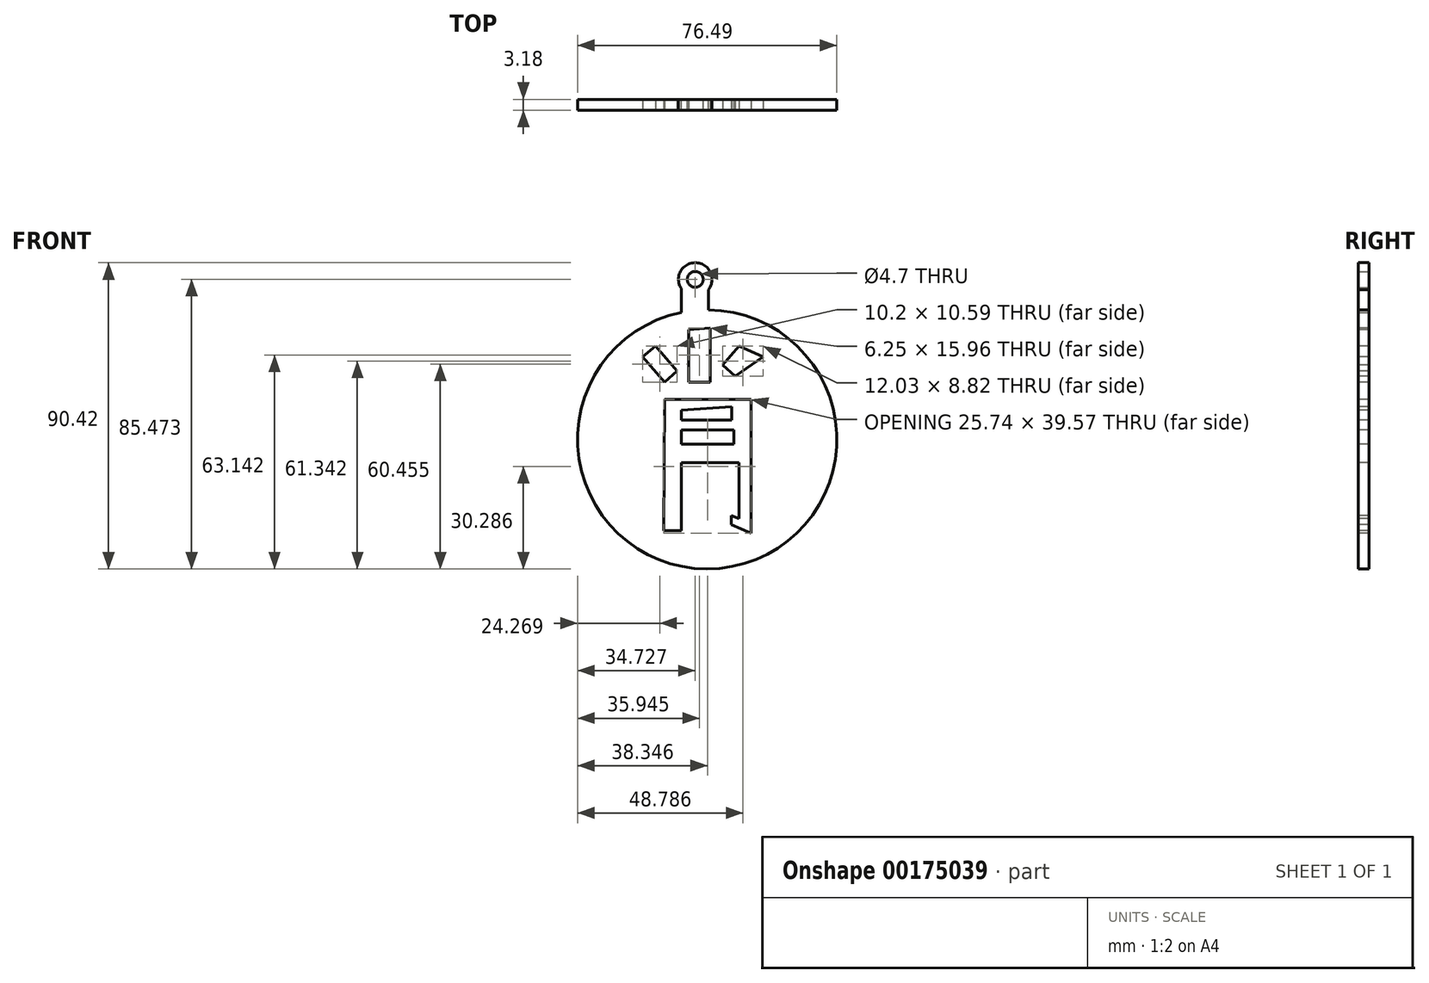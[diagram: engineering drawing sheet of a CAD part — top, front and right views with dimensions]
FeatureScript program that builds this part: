
annotation { "Feature Type Name" : "Feature", "Feature Type Description" : "" }
export const myFeature = defineFeature(function(context is Context, id is Id, definition is map)
    precondition{}
    {
        {
            var Q0;
            Q0=qCreatedBy(makeId("Front.planeOp"),FACE);
            var sketch = newSketch(context, id + "F0", { "sketchPlane" : qUnion([Q0])});
            skCircle(sketch, "E0", {"center": v(39.43, 36.64) * mm, "radius": 38.25 * mm});
            skLineSegment(sketch, "E1", {"start": v(31.77, 74.12) * mm, "end": v(31.77, 81.17) * mm});
            skLineSegment(sketch, "E2", {"start": v(39.78, 74.89) * mm, "end": v(39.78, 80.8) * mm});
            skCircle(sketch, "E3", {"center": v(35.9, 83.87) * mm, "radius": 4.94 * mm});
            skCircle(sketch, "E4", {"center": v(35.9, 83.87) * mm, "radius": 2.35 * mm});
            skSolve(sketch);
        }
        {
            var Q0;
            Q0 = qSketchRegion(id + "F0", true);
            extrude(context, id + "F1", {"entities" : qUnion([Q0]), "depth" : 3.17 * mm});
        }
        {
            var Q0;
            Q0=makeQuery(id+"F1.opExtrude","CAP_FACE",FACE,{"disambiguationData":[OSD([sQuery(id+"F0.wireOp",EDGE,"E0"),sQuery(id+"F0.wireOp",EDGE,"E1"),sQuery(id+"F0.wireOp",EDGE,"E2"),sQuery(id+"F0.wireOp",EDGE,"E3"),sQuery(id+"F0.wireOp",EDGE,"E4")])],"isStart":false});
            var sketch = newSketch(context, id + "F2", { "sketchPlane" : qUnion([Q0])});
            skLineSegment(sketch, "E5", {"start": v(20.35, 60.96) * mm, "end": v(26.83, 53.56) * mm});
            skLineSegment(sketch, "E6", {"start": v(26.83, 53.56) * mm, "end": v(30.55, 56.81) * mm});
            skLineSegment(sketch, "E7", {"start": v(30.55, 56.81) * mm, "end": v(24.13, 64.15) * mm});
            skLineSegment(sketch, "E8", {"start": v(24.13, 64.15) * mm, "end": v(20.35, 60.96) * mm});
            skLineSegment(sketch, "E9", {"start": v(34, 69.06) * mm, "end": v(34, 53.56) * mm});
            skLineSegment(sketch, "E10", {"start": v(34, 53.56) * mm, "end": v(40.25, 53.56) * mm});
            skLineSegment(sketch, "E11", {"start": v(40.25, 53.56) * mm, "end": v(40.25, 69.52) * mm});
            skLineSegment(sketch, "E12", {"start": v(40.25, 69.52) * mm, "end": v(34, 69.06) * mm});
            skLineSegment(sketch, "E13", {"start": v(48.8, 64.15) * mm, "end": v(43.95, 58.65) * mm});
            skLineSegment(sketch, "E14", {"start": v(43.95, 58.65) * mm, "end": v(47.7, 55.33) * mm});
            skLineSegment(sketch, "E15", {"start": v(47.7, 55.33) * mm, "end": v(55.98, 60.96) * mm});
            skLineSegment(sketch, "E16", {"start": v(55.98, 60.96) * mm, "end": v(48.8, 64.15) * mm});
            skLineSegment(sketch, "E17", {"start": v(26.83, 48.47) * mm, "end": v(52.4, 48.47) * mm});
            skPoint(sketch, "E17.endSnap0", {"position": v(52.4, 62.56) * mm});
            skLineSegment(sketch, "E18", {"start": v(52.4, 48.47) * mm, "end": v(52.4, 8.9) * mm});
            skLineSegment(sketch, "E19", {"start": v(52.4, 8.9) * mm, "end": v(46.55, 11.5) * mm});
            skLineSegment(sketch, "E20", {"start": v(46.55, 11.5) * mm, "end": v(46.55, 14.23) * mm});
            skLineSegment(sketch, "E21", {"start": v(46.55, 14.23) * mm, "end": v(48.8, 13.22) * mm});
            skLineSegment(sketch, "E22", {"start": v(48.8, 13.22) * mm, "end": v(48.8, 29.73) * mm});
            skLineSegment(sketch, "E23", {"start": v(48.8, 29.73) * mm, "end": v(31.77, 29.73) * mm});
            skLineSegment(sketch, "E24", {"start": v(31.77, 29.73) * mm, "end": v(31.77, 9.68) * mm});
            skLineSegment(sketch, "E25", {"start": v(31.77, 9.68) * mm, "end": v(26.66, 9.68) * mm});
            skLineSegment(sketch, "E26", {"start": v(26.66, 9.68) * mm, "end": v(26.83, 48.47) * mm});
            skLineSegment(sketch, "E27", {"start": v(31.77, 35.29) * mm, "end": v(47.27, 35.29) * mm});
            skLineSegment(sketch, "E28", {"start": v(47.27, 35.29) * mm, "end": v(47.27, 39.38) * mm});
            skLineSegment(sketch, "E29", {"start": v(47.27, 39.38) * mm, "end": v(31.77, 39.38) * mm});
            skLineSegment(sketch, "E30", {"start": v(31.77, 39.38) * mm, "end": v(31.77, 35.29) * mm});
            skLineSegment(sketch, "E31", {"start": v(31.77, 45.27) * mm, "end": v(31.77, 42.32) * mm});
            skLineSegment(sketch, "E32", {"start": v(31.77, 42.32) * mm, "end": v(46.62, 42.32) * mm});
            skLineSegment(sketch, "E33", {"start": v(46.62, 42.32) * mm, "end": v(46.62, 46.25) * mm});
            skLineSegment(sketch, "E34", {"start": v(46.62, 46.25) * mm, "end": v(31.77, 45.27) * mm});
            skLineSegment(sketch, "E35", {"start": v(36.15, 35.29) * mm, "end": v(34.36, 35.29) * mm});
            skPoint(sketch, "E36.startSnap0", {"position": v(39.52, 39.38) * mm});
            skSolve(sketch);
        }
        {
            var Q0;
            Q0=makeQuery(id+"F2.imprint","IMPRINT",FACE,{"disambiguationData":[TD([[makeQuery(id+"F2.imprint","IMPRINT",EDGE,{"derivedFrom":sQuery(id+"F2.wireOp",EDGE,"E5")}),1.0]])]});
            var Q1;
            Q1=makeQuery(id+"F2.imprint","IMPRINT",FACE,{"disambiguationData":[TD([[makeQuery(id+"F2.imprint","IMPRINT",EDGE,{"derivedFrom":sQuery(id+"F2.wireOp",EDGE,"E9")}),1.0]])]});
            var Q2;
            Q2=makeQuery(id+"F2.imprint","IMPRINT",FACE,{"disambiguationData":[TD([[makeQuery(id+"F2.imprint","IMPRINT",EDGE,{"derivedFrom":sQuery(id+"F2.wireOp",EDGE,"E13")}),1.0]])]});
            var Q3;
            Q3=makeQuery(id+"F2.imprint","IMPRINT",FACE,{"disambiguationData":[TD([[makeQuery(id+"F2.imprint","IMPRINT",EDGE,{"derivedFrom":sQuery(id+"F2.wireOp",EDGE,"E17")}),-1.0]])]});
            var Q4;
            {var subQ0=sQuery(id+"F2.wireOp",EDGE,"aVBbDBSk-wFVR-j3cv-Srhj-Kdv2nJzsByz3");Q4=makeQuery(id+"F2.imprint","IMPRINT",FACE,{"disambiguationData":[TD([[makeQuery(id+"F2.imprint","IMPRINT",EDGE,{"derivedFrom":subQ0}),1.0]])]});}
            var Q5;
            {var subQ0=sQuery(id+"F2.wireOp",EDGE,"VGyFq3D9-xVgg-vz6W-n4dS-cXjDcoi1llOh");Q5=makeQuery(id+"F2.imprint","IMPRINT",FACE,{"disambiguationData":[TD([[makeQuery(id+"F2.imprint","IMPRINT",EDGE,{"derivedFrom":subQ0}),1.0]])]});}
            var Q6;
            Q6=makeQuery(id+"F2.imprint","IMPRINT",FACE,{"disambiguationData":[TD([[makeQuery(id+"F2.imprint","IMPRINT",EDGE,{"derivedFrom":sQuery(id+"F2.wireOp",EDGE,"E36")}),1.0]])]});
            var Q7;
            Q7=makeQuery(id+"F2.imprint","IMPRINT",FACE,{"disambiguationData":[TD([[makeQuery(id+"F2.imprint","IMPRINT",EDGE,{"derivedFrom":sQuery(id+"F2.wireOp",EDGE,"clj0EBL0-pKll-iuWl-9nAF-mdBS2kUrVhOE")}),-1.0]])]});
            extrude(context, id + "F3", {"entities" : qUnion([Q0, Q1, Q2, Q3, Q4, Q5, Q6, Q7]), "operationType" : NewBodyOperationType.REMOVE, "oppositeDirection" : true, "depth" : 3.17 * mm});
        }
    });
